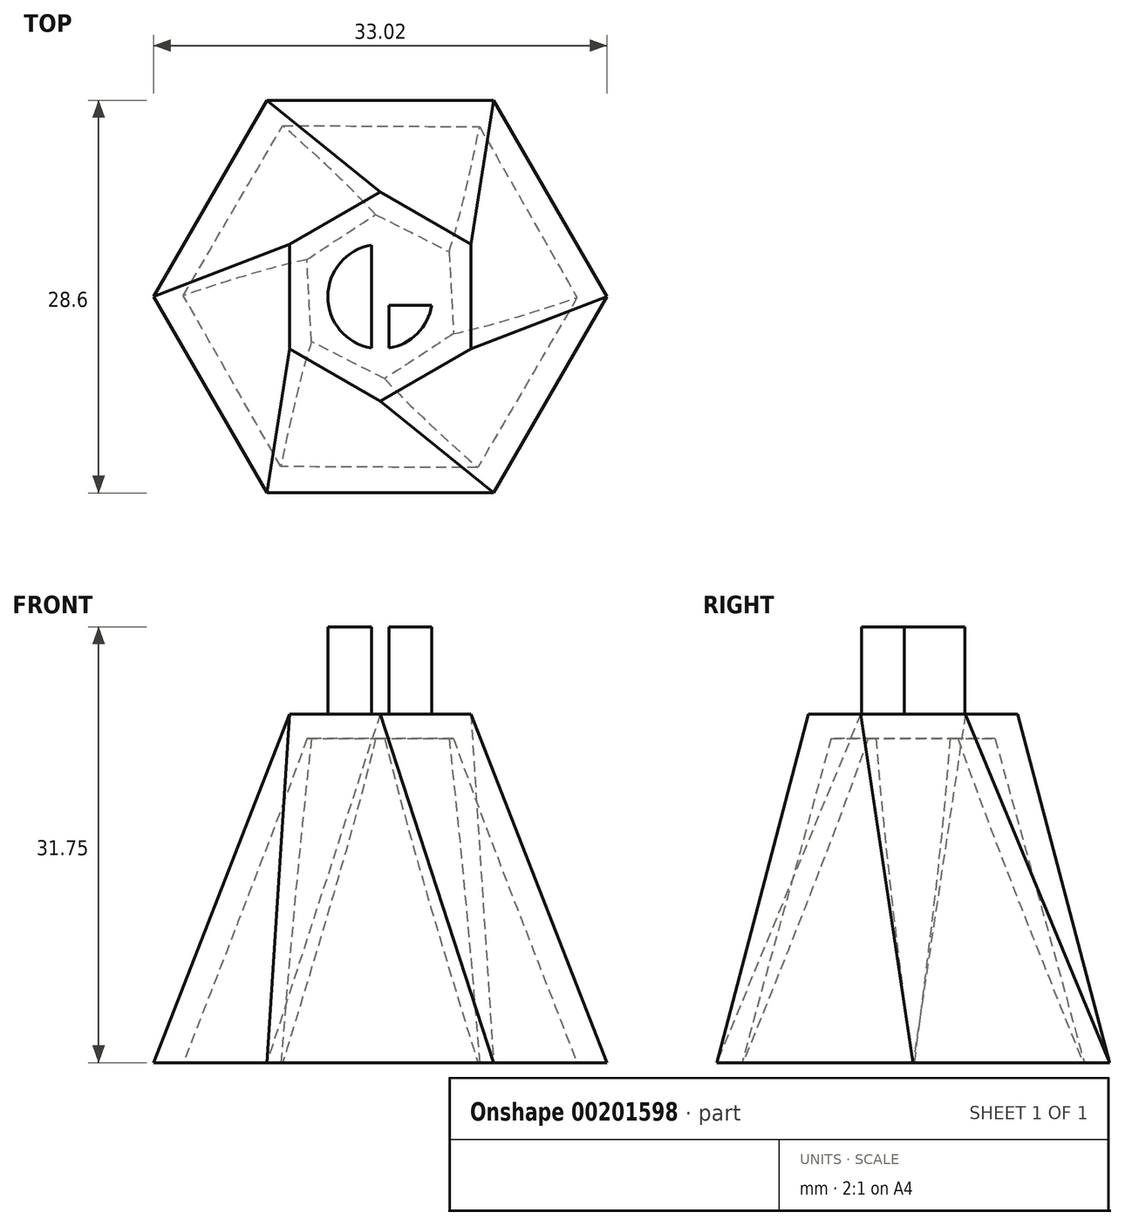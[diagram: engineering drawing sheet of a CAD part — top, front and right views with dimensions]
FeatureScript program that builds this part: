
annotation { "Feature Type Name" : "Feature", "Feature Type Description" : "" }
export const myFeature = defineFeature(function(context is Context, id is Id, definition is map)
    precondition{}
    {
        {
            var Q0;
            Q0=qCreatedBy(makeId("Top.planeOp"),FACE);
            var sketch = newSketch(context, id + "F0", { "sketchPlane" : qUnion([Q0])});
            skCircle(sketch, "E0.cCircle", {"center": v(0, 0) * mm, "radius": 14.3 * mm, "construction": true});
            skLineSegment(sketch, "E0.0", {"start": v(-8.26, 14.3) * mm, "end": v(8.26, 14.3) * mm});
            skLineSegment(sketch, "E0.1", {"start": v(8.26, 14.3) * mm, "end": v(16.51, 0) * mm});
            skLineSegment(sketch, "E0.2", {"start": v(16.5, 0) * mm, "end": v(8.26, -14.3) * mm});
            skLineSegment(sketch, "E0.3", {"start": v(8.26, -14.3) * mm, "end": v(-8.25, -14.3) * mm});
            skLineSegment(sketch, "E0.4", {"start": v(-8.25, -14.3) * mm, "end": v(-16.51, 0) * mm});
            skLineSegment(sketch, "E0.5", {"start": v(-16.51, 0) * mm, "end": v(-8.26, 14.3) * mm});
            skPoint(sketch, "E0.0.midPoint", {"position": v(0, 14.3) * mm});
            skSolve(sketch);
        }
        {
            var Q0;
            Q0=qCreatedBy(makeId("Top.planeOp"),FACE);
            cPlane(context, id + "F1", {"entities" : qUnion([Q0]), "cplaneType" : CPlaneType.OFFSET, "offset" : 25.4 * mm, "width" : 152.4 * mm, "height" : 152.4 * mm});
        }
        {
            var Q0;
            Q0=qCreatedBy(id+"F1.planeOp",FACE);
            var sketch = newSketch(context, id + "F2", { "sketchPlane" : qUnion([Q0])});
            skCircle(sketch, "E1.cCircle", {"center": v(0, 0) * mm, "radius": 6.6 * mm, "construction": true});
            skLineSegment(sketch, "E1.0", {"start": v(-6.6, 3.81) * mm, "end": v(0, 7.62) * mm});
            skLineSegment(sketch, "E1.1", {"start": v(0, 7.62) * mm, "end": v(6.6, 3.81) * mm});
            skLineSegment(sketch, "E1.2", {"start": v(6.6, 3.8) * mm, "end": v(6.6, -3.81) * mm});
            skLineSegment(sketch, "E1.3", {"start": v(6.6, -3.81) * mm, "end": v(0, -7.62) * mm});
            skLineSegment(sketch, "E1.4", {"start": v(0, -7.62) * mm, "end": v(-6.6, -3.8) * mm});
            skLineSegment(sketch, "E1.5", {"start": v(-6.6, -3.8) * mm, "end": v(-6.6, 3.81) * mm});
            skPoint(sketch, "E1.0.midPoint", {"position": v(-3.3, 5.71) * mm});
            skSolve(sketch);
        }
        {
            var Q0;
            Q0=makeQuery(id+"F2.imprint","IMPRINT",FACE,{"disambiguationData":[TD([[makeQuery(id+"F2.imprint","IMPRINT",EDGE,{"derivedFrom":sQuery(id+"F2.wireOp",EDGE,"E1.0")}),-1.0]])]});
            var Q1;
            Q1=makeQuery(id+"F0.imprint","IMPRINT",FACE,{"disambiguationData":[TD([[makeQuery(id+"F0.imprint","IMPRINT",EDGE,{"derivedFrom":sQuery(id+"F0.wireOp",EDGE,"E0.0")}),-1.0]])]});
            loft(context, id + "F3", {"sheetProfilesArray" : [{ "sheetProfileEntities" : qUnion([Q0]) }, { "sheetProfileEntities" : qUnion([Q1]) }]});
        }
        {
            var Q0;
            Q0=makeQuery(id+"F3.opLoft","CAP_FACE",FACE,{"disambiguationData":[OSD([makeQuery(id+"F0.imprint","IMPRINT",FACE,{"disambiguationData":[TD([[makeQuery(id+"F0.imprint","IMPRINT",EDGE,{"derivedFrom":sQuery(id+"F0.wireOp",EDGE,"E0.0")}),-1.0]])]})])],"isStart":true});
            shell(context, id + "F4", {"entities" : qUnion([Q0]), "thickness" : 1.78 * mm});
        }
        {
            var Q0;
            Q0=makeQuery(id+"F3.opLoft","CAP_FACE",FACE,{"disambiguationData":[OSD([makeQuery(id+"F2.imprint","IMPRINT",FACE,{"disambiguationData":[TD([[makeQuery(id+"F2.imprint","IMPRINT",EDGE,{"derivedFrom":sQuery(id+"F2.wireOp",EDGE,"E1.0")}),-1.0]])]})])],"isStart":true});
            var sketch = newSketch(context, id + "F5", { "sketchPlane" : qUnion([Q0])});
            skCircle(sketch, "E2", {"center": v(0, 0) * mm, "radius": 3.81 * mm});
            skLineSegment(sketch, "E3.bottom", {"start": v(-0.63, 3.81) * mm, "end": v(0.64, 3.81) * mm});
            skLineSegment(sketch, "E3.top", {"start": v(-0.64, -3.81) * mm, "end": v(0.63, -3.81) * mm});
            skLineSegment(sketch, "E3.left", {"start": v(-0.63, 3.81) * mm, "end": v(-0.64, -3.81) * mm});
            skLineSegment(sketch, "E3.right", {"start": v(0.64, 3.81) * mm, "end": v(0.63, -3.81) * mm});
            skLineSegment(sketch, "E4.bottom", {"start": v(-3.81, 0.64) * mm, "end": v(3.81, 0.64) * mm});
            skLineSegment(sketch, "E4.top", {"start": v(-3.81, -0.64) * mm, "end": v(3.81, -0.64) * mm});
            skLineSegment(sketch, "E4.left", {"start": v(-3.81, 0.64) * mm, "end": v(-3.81, -0.64) * mm});
            skLineSegment(sketch, "E4.right", {"start": v(3.81, 0.64) * mm, "end": v(3.81, -0.64) * mm});
            skSolve(sketch);
        }
        {
            var Q0;
            {var subQ0=sQuery(id+"F5.wireOp",EDGE,"E3.left");var subQ1=sQuery(id+"F5.wireOp",EDGE,"E2");var subQ2=makeQuery(id+"F5.imprint","INTERSECT",VERTEX,{"disambiguationData":[OD(0.0)],"derivedFrom":[subQ1,subQ0]});Q0=makeQuery(id+"F5.imprint","IMPRINT",FACE,{"disambiguationData":[TD([[makeQuery(id+"F5.imprint","IMPRINT",EDGE,{"disambiguationData":[TD([[subQ2,-1.0]])],"derivedFrom":subQ1}),1.0]])]});}
            var Q1;
            {var subQ0=sQuery(id+"F5.wireOp",EDGE,"E4.bottom");var subQ1=sQuery(id+"F5.wireOp",EDGE,"E2");var subQ2=makeQuery(id+"F5.imprint","INTERSECT",VERTEX,{"disambiguationData":[OD(0.0)],"derivedFrom":[subQ1,subQ0]});Q1=makeQuery(id+"F5.imprint","IMPRINT",FACE,{"disambiguationData":[TD([[makeQuery(id+"F5.imprint","IMPRINT",EDGE,{"disambiguationData":[TD([[subQ2,-1.0]])],"derivedFrom":subQ1}),1.0]])]});}
            var Q2;
            {var subQ0=sQuery(id+"F5.wireOp",EDGE,"E3.right");var subQ1=sQuery(id+"F5.wireOp",EDGE,"E2");var subQ2=makeQuery(id+"F5.imprint","INTERSECT",VERTEX,{"disambiguationData":[OD(1.0)],"derivedFrom":[subQ1,subQ0]});Q2=makeQuery(id+"F5.imprint","IMPRINT",FACE,{"disambiguationData":[TD([[makeQuery(id+"F5.imprint","IMPRINT",EDGE,{"disambiguationData":[TD([[subQ2,-1.0]])],"derivedFrom":subQ1}),1.0]])]});}
            var Q3;
            {var subQ0=sQuery(id+"F5.wireOp",EDGE,"E4.top");var subQ1=sQuery(id+"F5.wireOp",EDGE,"E2");var subQ2=makeQuery(id+"F5.imprint","INTERSECT",VERTEX,{"disambiguationData":[OD(0.0)],"derivedFrom":[subQ1,subQ0]});Q3=makeQuery(id+"F5.imprint","IMPRINT",FACE,{"disambiguationData":[TD([[makeQuery(id+"F5.imprint","IMPRINT",EDGE,{"disambiguationData":[TD([[subQ2,-1.0]])],"derivedFrom":subQ1}),1.0]])]});}
            extrude(context, id + "F6", {"entities" : qUnion([Q0, Q1, Q2, Q3]), "operationType" : NewBodyOperationType.ADD, "depth" : 6.35 * mm});
        }
    });
